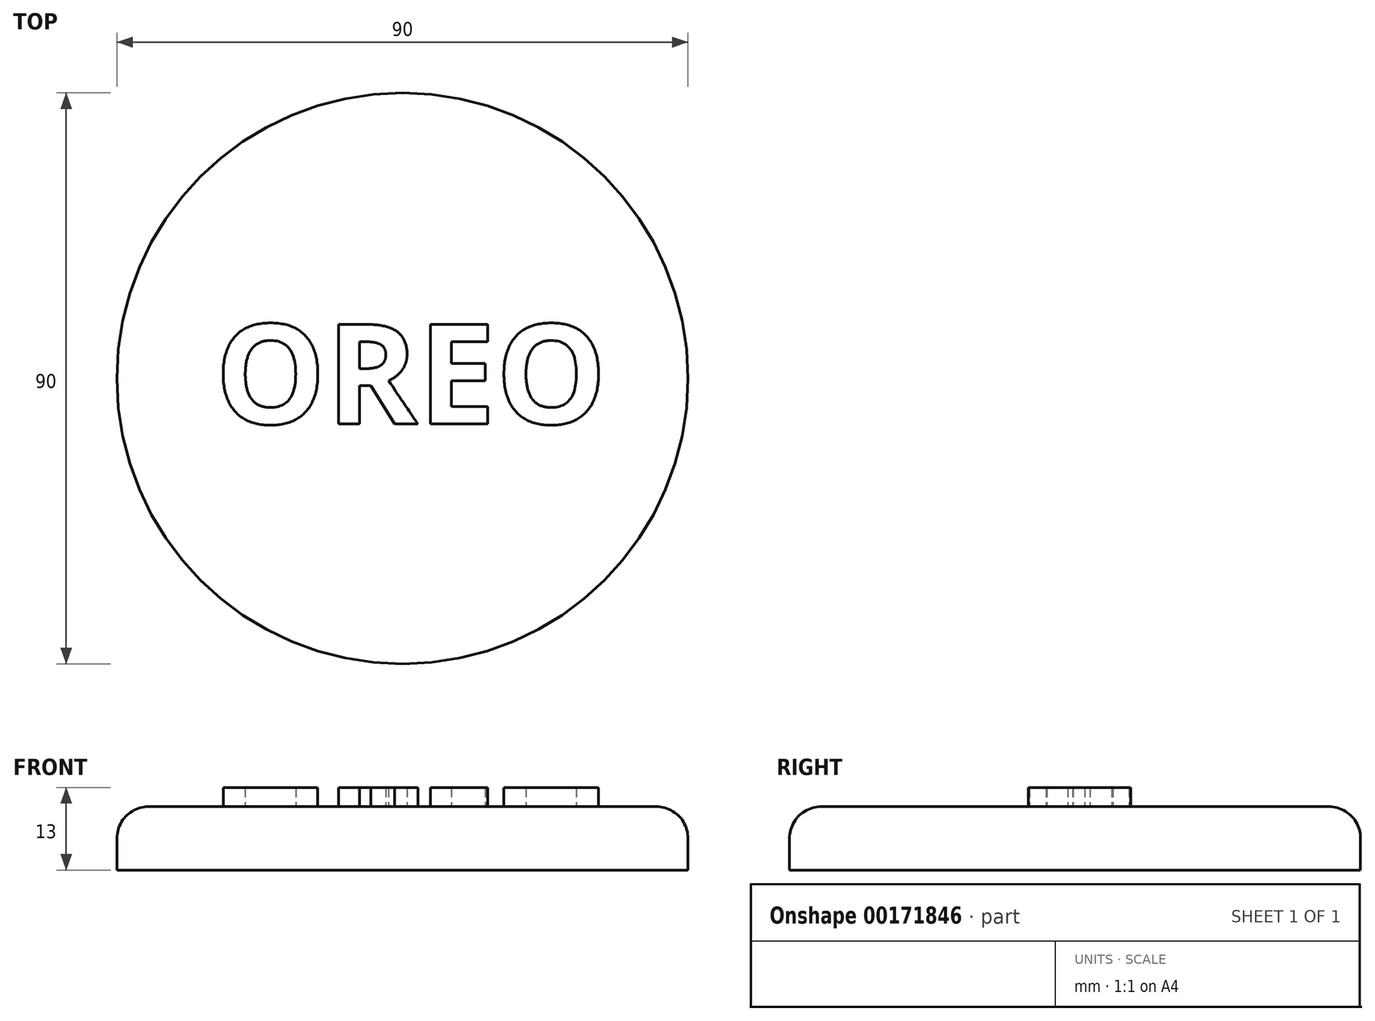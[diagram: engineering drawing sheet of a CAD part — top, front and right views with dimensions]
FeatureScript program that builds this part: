
annotation { "Feature Type Name" : "Feature", "Feature Type Description" : "" }
export const myFeature = defineFeature(function(context is Context, id is Id, definition is map)
    precondition{}
    {
        {
            var Q0;
            Q0=qCreatedBy(makeId("Top.planeOp"),FACE);
            var sketch = newSketch(context, id + "F0", { "sketchPlane" : qUnion([Q0])});
            skCircle(sketch, "E0", {"center": v(0, 0) * mm, "radius": 45 * mm});
            skSolve(sketch);
        }
        {
            var Q0;
            Q0=qSketchRegion(id+"F0",true);
            extrude(context, id + "F1", {"entities" : qUnion([Q0]), "oppositeDirection" : true, "depth" : 10 * mm});
        }
        {
            var Q0;
            Q0=makeQuery(id+"F1.opExtrude","CAP_FACE",FACE,{"disambiguationData":[OSD([sQuery(id+"F0.wireOp",EDGE,"E0")])],"isStart":true});
            fillet(context, id + "F2", {"entities" : qUnion([Q0]), "radius" : 5 * mm, "tangentPropagation" : true, "allowEdgeOverflow" : false});
        }
        {
            var Q0;
            Q0=makeQuery(id+"F1.opExtrude","CAP_FACE",FACE,{"disambiguationData":[OSD([sQuery(id+"F0.wireOp",EDGE,"E0")])],"isStart":true});
            var sketch = newSketch(context, id + "F3", { "sketchPlane" : qUnion([Q0])});
            skText(sketch, "E1", { "text": "OREO\n", "fontName": "OpenSans-Bold.ttf"});
            const initialGuessF3  = {"E1": [-0.02953, -0.00716, 1, 0, 0.0158]};
            skSetInitialGuess(sketch, initialGuessF3);
            skSolve(sketch);
        }
        {
            var Q0;
            Q0=qSketchRegion(id+"F3",true);
            extrude(context, id + "F4", {"entities" : qUnion([Q0]), "operationType" : NewBodyOperationType.ADD, "depth" : 3 * mm});
        }
    });
